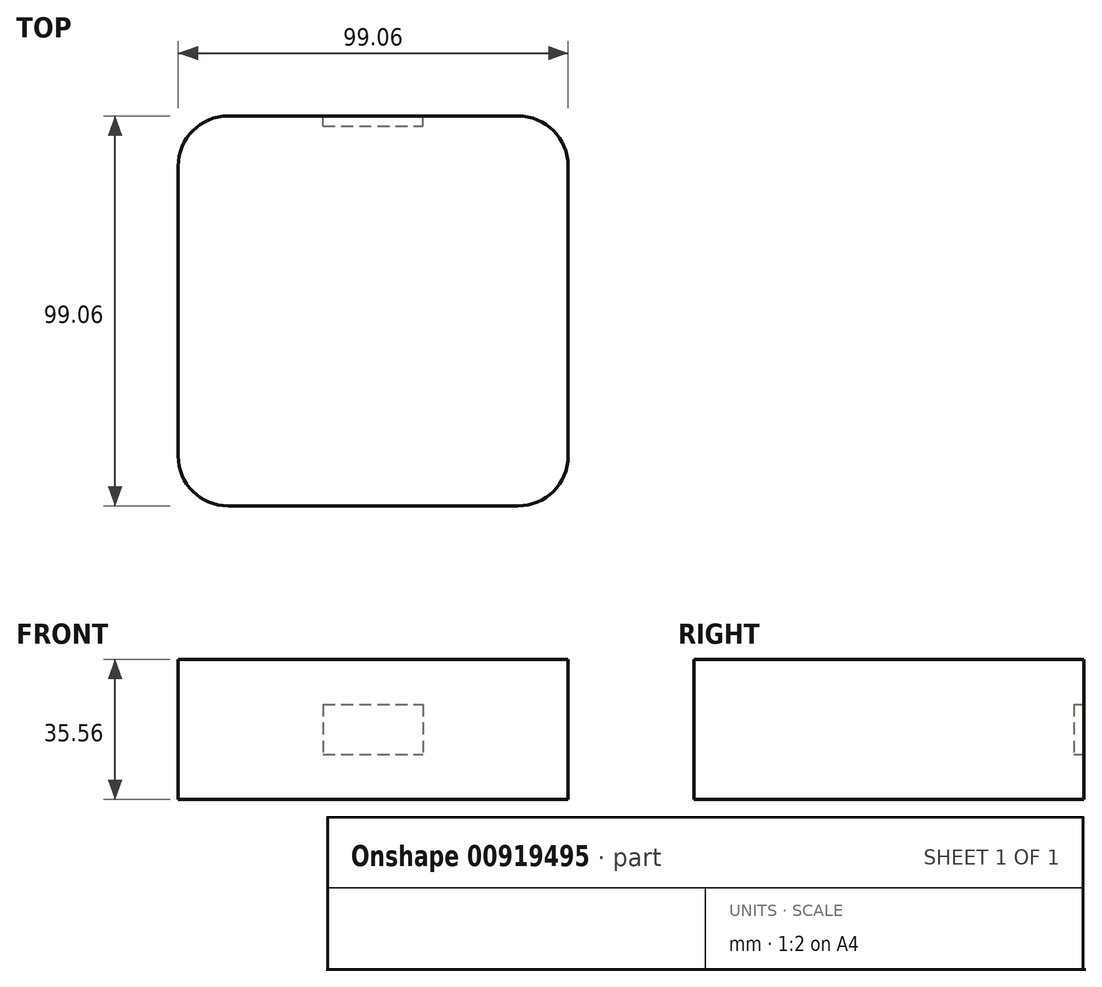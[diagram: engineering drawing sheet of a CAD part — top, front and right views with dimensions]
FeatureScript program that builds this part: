
annotation { "Feature Type Name" : "Feature", "Feature Type Description" : "" }
export const myFeature = defineFeature(function(context is Context, id is Id, definition is map)
    precondition{}
    {
        {
            var Q0;
            Q0=qCreatedBy(makeId("Top.planeOp"),FACE);
            var sketch = newSketch(context, id + "F0", { "sketchPlane" : qUnion([Q0])});
            skLineSegment(sketch, "E0.bottom", {"start": v(49.53, 49.53) * mm, "end": v(-49.53, 49.53) * mm});
            skLineSegment(sketch, "E0.top", {"start": v(49.53, -49.53) * mm, "end": v(-49.53, -49.53) * mm});
            skLineSegment(sketch, "E0.left", {"start": v(49.53, 49.53) * mm, "end": v(49.53, -49.53) * mm});
            skLineSegment(sketch, "E0.right", {"start": v(-49.53, 49.53) * mm, "end": v(-49.53, -49.53) * mm});
            skPoint(sketch, "E0.middle", {"position": v(0, 0) * mm});
            skSolve(sketch);
        }
        {
            var Q0;
            Q0=makeQuery(id+"F0.imprint","IMPRINT",FACE,{"disambiguationData":[TD([[makeQuery(id+"F0.imprint","IMPRINT",EDGE,{"derivedFrom":sQuery(id+"F0.wireOp",EDGE,"E0.bottom")}),1.0]])]});
            extrude(context, id + "F1", {"entities" : qUnion([Q0]), "depth" : 35.56 * mm, "offsetDistance" : 25.4 * mm});
        }
        {
            var Q0;
            Q0=makeQuery(id+"F1.opExtrude","SWEPT_EDGE",EDGE,{"disambiguationData":[OSD([sQuery(id+"F0.wireOp",EDGE,"E0.top"),sQuery(id+"F0.wireOp",EDGE,"E0.left")])]});
            var Q1;
            Q1=makeQuery(id+"F1.opExtrude","SWEPT_EDGE",EDGE,{"disambiguationData":[OSD([sQuery(id+"F0.wireOp",EDGE,"E0.bottom"),sQuery(id+"F0.wireOp",EDGE,"E0.left")])]});
            var Q2;
            Q2=makeQuery(id+"F1.opExtrude","SWEPT_EDGE",EDGE,{"disambiguationData":[OSD([sQuery(id+"F0.wireOp",EDGE,"E0.top"),sQuery(id+"F0.wireOp",EDGE,"E0.right")])]});
            var Q3;
            Q3=makeQuery(id+"F1.opExtrude","SWEPT_EDGE",EDGE,{"disambiguationData":[OSD([sQuery(id+"F0.wireOp",EDGE,"E0.bottom"),sQuery(id+"F0.wireOp",EDGE,"E0.right")])]});
            fillet(context, id + "F2", {"entities" : qUnion([Q0, Q1, Q2, Q3]), "radius" : 12.7 * mm, "tangentPropagation" : true, "allowEdgeOverflow" : false});
        }
        {
            var Q0;
            Q0=makeQuery(id+"F1.opExtrude","SWEPT_FACE",FACE,{"disambiguationData":[OSD([sQuery(id+"F0.wireOp",EDGE,"E0.bottom")])]});
            var sketch = newSketch(context, id + "F3", { "sketchPlane" : qUnion([Q0])});
            skLineSegment(sketch, "E1", {"start": v(0, 0) * mm, "end": v(0, 35.56) * mm, "construction": true});
            skLineSegment(sketch, "E2.bottom", {"start": v(12.7, 24.13) * mm, "end": v(-12.7, 24.13) * mm});
            skLineSegment(sketch, "E2.top", {"start": v(12.7, 11.43) * mm, "end": v(-12.7, 11.43) * mm});
            skLineSegment(sketch, "E2.left", {"start": v(12.7, 24.13) * mm, "end": v(12.7, 11.43) * mm});
            skLineSegment(sketch, "E2.right", {"start": v(-12.7, 24.13) * mm, "end": v(-12.7, 11.43) * mm});
            skPoint(sketch, "E2.middle", {"position": v(0, 17.78) * mm});
            skSolve(sketch);
        }
        {
            var Q0;
            Q0=makeQuery(id+"F3.imprint","IMPRINT",FACE,{"disambiguationData":[TD([[makeQuery(id+"F3.imprint","IMPRINT",EDGE,{"derivedFrom":sQuery(id+"F3.wireOp",EDGE,"E2.bottom")}),1.0]])]});
            extrude(context, id + "F4", {"entities" : qUnion([Q0]), "operationType" : NewBodyOperationType.REMOVE, "oppositeDirection" : true, "depth" : 2.54 * mm, "offsetDistance" : 25.4 * mm});
        }
    });
